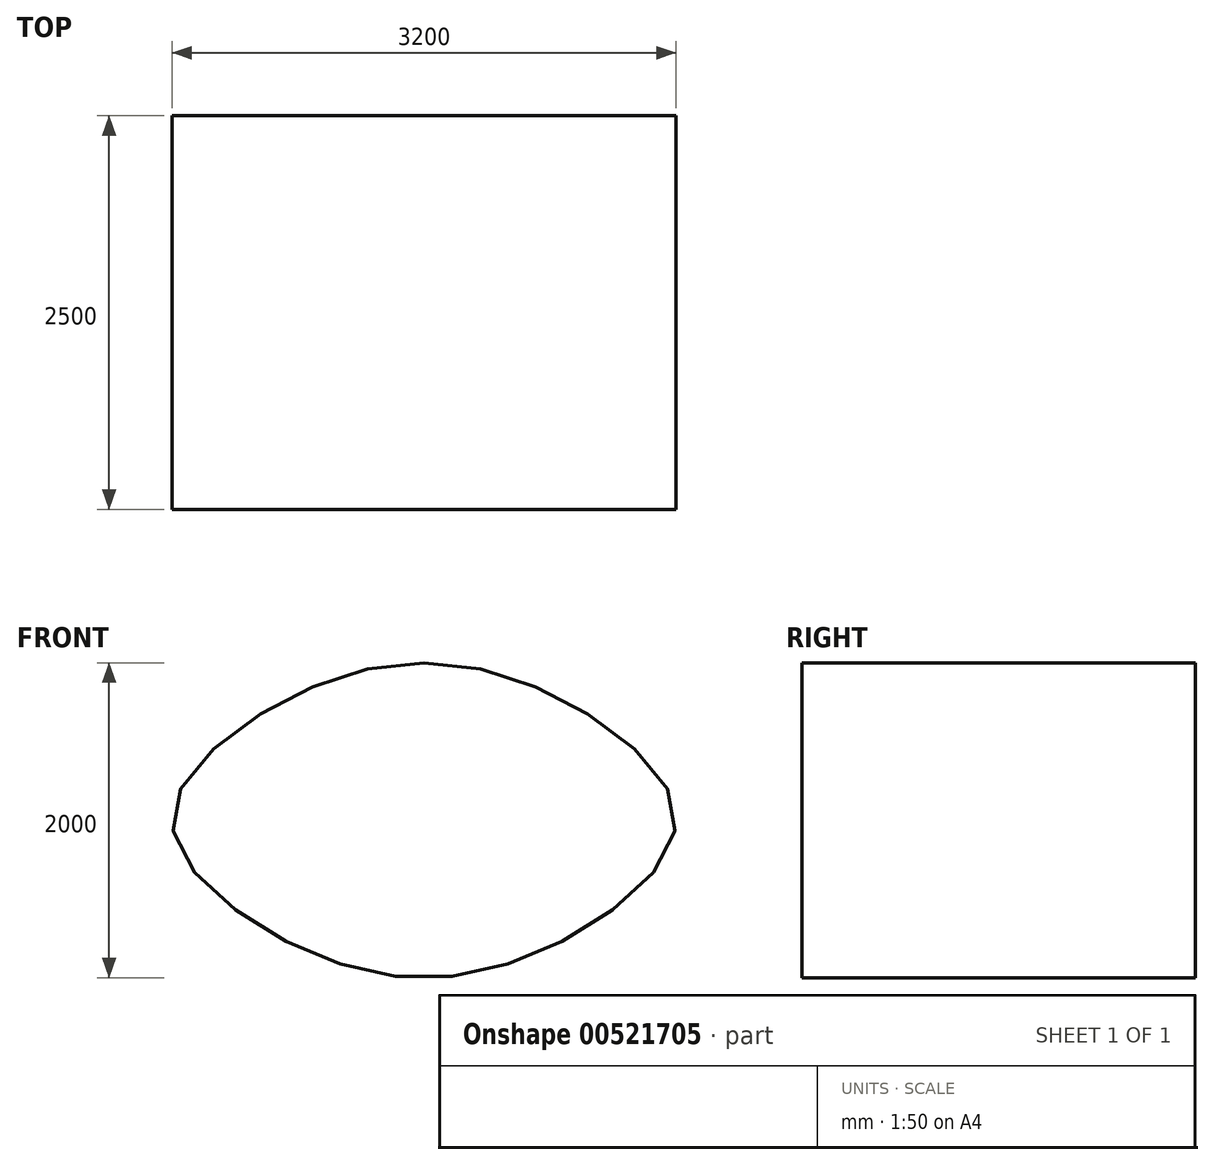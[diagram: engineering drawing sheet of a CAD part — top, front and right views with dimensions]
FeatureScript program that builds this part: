
annotation { "Feature Type Name" : "Feature", "Feature Type Description" : "" }
export const myFeature = defineFeature(function(context is Context, id is Id, definition is map)
    precondition{}
    {
        {
            var Q0;
            Q0=qCreatedBy(makeId("Front.planeOp"),FACE);
            var sketch = newSketch(context, id + "F0", { "sketchPlane" : qUnion([Q0])});
            skPoint(sketch, "E0.middle", {"position": v(0, 0) * mm});
            skFitSpline(sketch, "E1", {"points": [v(0, 1000) * mm, v(1060, 662.5) * mm, v(1600, 0) * mm, v(1060, -662.5) * mm, v(0, -1000) * mm, v(-1060, -662.5) * mm, v(-1600, 0) * mm, v(-1060, 662.5) * mm, v(0, 1000) * mm]});
            skSolve(sketch);
        }
        {
            var Q0;
            Q0=makeQuery(id+"F0.imprint","IMPRINT",FACE,{"disambiguationData":[TD([[makeQuery(id+"F0.imprint","IMPRINT",EDGE,{"derivedFrom":sQuery(id+"F0.wireOp",EDGE,"E1")}),-1.0]])]});
            extrude(context, id + "F1", {"entities" : qUnion([Q0]), "endBound" : BoundingType.SYMMETRIC, "depth" : 2500 * mm, "offsetDistance" : 25 * mm});
        }
    });
